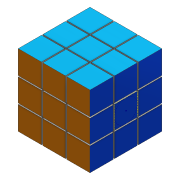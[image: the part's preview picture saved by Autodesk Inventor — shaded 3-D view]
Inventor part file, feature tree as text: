
AUTODESK INVENTOR PART (.ipt)
format: ipt  version: 2016 (Build 200138000, 138)  size: 334,336 bytes
history: native  units: mm
features: sketch x7, extrude x6, mirror x4, plane x3, pattern_circular x3, projected_geometry x1
ambient origin geometry x8: Origin, YZ Plane, XZ Plane, XY Plane, X Axis, Y Axis, Z Axis, Center Point
bodies: 实体1 (feature_tree)
feature tree (24):
  extrude  "拉伸1"  Depth=57.0mm TaperAngle=0.0deg
  extrude  "拉伸2"  Depth=1.0mm
  mirror  "镜像1"
  extrude  "拉伸3"  Depth=18.5mm
  plane  "工作平面1"
  mirror  "镜像2"
  pattern_circular  "环形阵列1"  Count=4 Angle=360.0deg
  pattern_circular  "环形阵列2"  Count=4 Angle=360.0deg
  extrude  "拉伸4"  Depth=1.0mm TaperAngle=360.0deg
  pattern_circular  "环形阵列3"  [2 undecoded]
  extrude  "拉伸5"  Depth=18.5mm
  mirror  "镜像3"
  extrude  "拉伸6"  Depth=1.0mm
  mirror  "镜像4"
  sketch  "草图8"  dims[d18=1.0mm d19=0.0mm d20=40.0mm d21=360.0deg d23=1.0mm d24=18.5mm d25=1.0mm d26=18.5mm d27=60.0mm d28=0.0mm d29=1.0mm d30=0.0mm]
  sketch  "草图1"  dims[d0=57.0mm d1=57.0mm d2=0.0mm]
  sketch  "草图2"  dims[d3=18.5mm d4=1.0mm]
  projected_geometry  "投影回路1"
  sketch  "草图3"  dims[d5=1.0mm d6=18.5mm]
  sketch  "草图4"  dims[d7=1.0mm d8=0.0mm]
  sketch  "草图5"  dims[d9=1.0mm d10=0.0mm]
  plane  "工作平面2"
  sketch  "草图6"  dims[d11=28.5mm d12=40.0mm d13=360.0deg d15=40.0mm d16=360.0deg]
  plane  "工作平面3"
note: 2 required parameter values undecoded (feature->parameter linkage not recoverable at this tier; creation-order binding heuristic only, values carry confidence <= 0.55)
